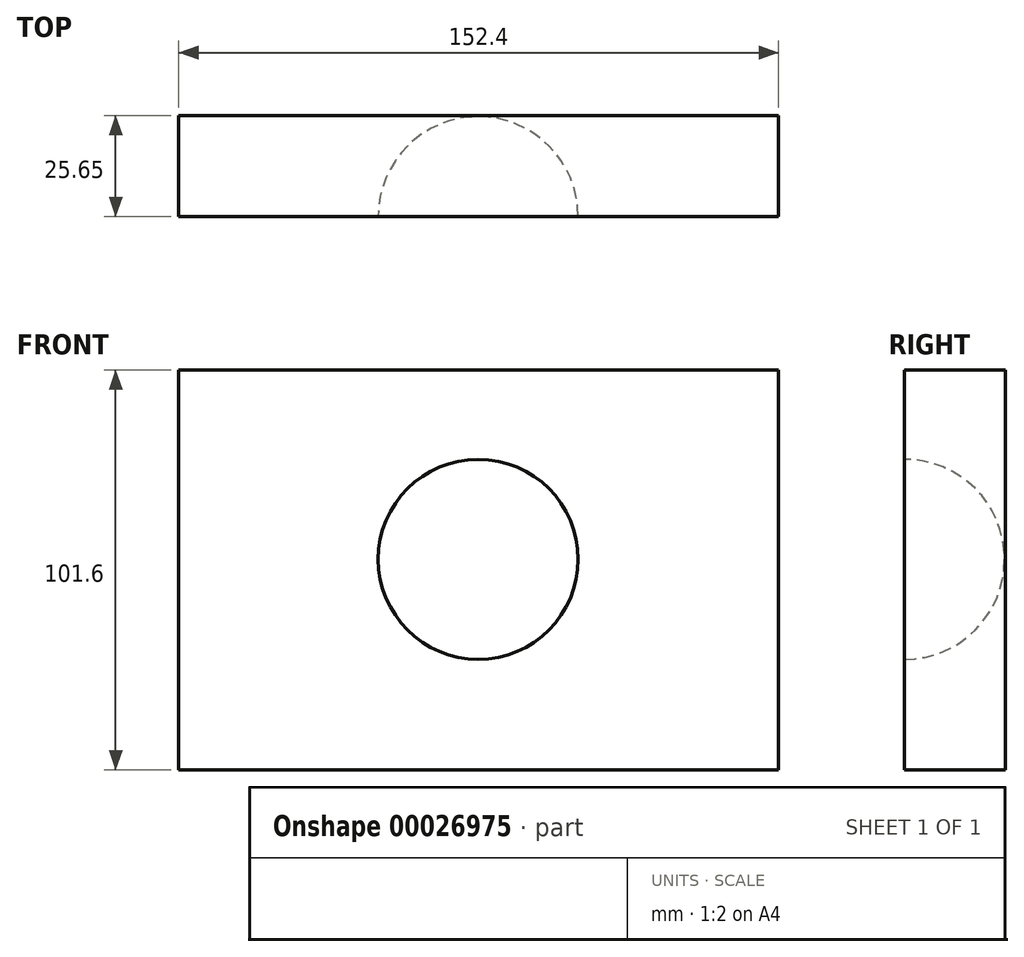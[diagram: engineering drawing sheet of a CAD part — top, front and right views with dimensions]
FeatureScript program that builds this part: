
annotation { "Feature Type Name" : "Feature", "Feature Type Description" : "" }
export const myFeature = defineFeature(function(context is Context, id is Id, definition is map)
    precondition{}
    {
        {
            var Q0;
            Q0=qCreatedBy(makeId("Front.planeOp"),FACE);
            var sketch = newSketch(context, id + "F0", { "sketchPlane" : qUnion([Q0])});
            skLineSegment(sketch, "E0.bottom", {"start": v(-74.85, 56.73) * mm, "end": v(77.55, 56.73) * mm});
            skLineSegment(sketch, "E0.top", {"start": v(-74.85, -44.87) * mm, "end": v(77.55, -44.87) * mm});
            skLineSegment(sketch, "E0.left", {"start": v(-74.85, 56.73) * mm, "end": v(-74.85, -44.87) * mm});
            skLineSegment(sketch, "E0.right", {"start": v(77.55, 56.73) * mm, "end": v(77.55, -44.87) * mm});
            skLineSegment(sketch, "E1", {"start": v(1.35, 23.81) * mm, "end": v(1.35, 23.8) * mm});
            skLineSegment(sketch, "E2.left", {"start": v(1.35, 23.8) * mm, "end": v(1.35, 23.81) * mm});
            skLineSegment(sketch, "E3.bottom", {"start": v(10.34, 5.93) * mm, "end": v(10.34, 5.93) * mm});
            skPoint(sketch, "E4.orphan", {"position": v(1.35, 5.93) * mm});
            skPoint(sketch, "E5.orphan", {"position": v(1.35, 56.73) * mm});
            skPoint(sketch, "E6.orphan", {"position": v(77.55, 5.93) * mm});
            skPoint(sketch, "E7.start.orphan", {"position": v(-74.85, 5.93) * mm});
            skPoint(sketch, "E8.trimOffspring.end.orphan", {"position": v(1.35, -44.87) * mm});
            skSolve(sketch);
        }
        {
            var Q0;
            Q0=makeQuery(id+"F0.imprint","IMPRINT",FACE,{"disambiguationData":[TD([[makeQuery(id+"F0.imprint","IMPRINT",EDGE,{"derivedFrom":sQuery(id+"F0.wireOp",EDGE,"E0.bottom")}),-1.0]])]});
            extrude(context, id + "F1", {"entities" : qUnion([Q0]), "oppositeDirection" : true, "depth" : 25.65 * mm});
        }
        {
            var Q0;
            Q0=makeQuery(id+"F0.imprint","IMPRINT",FACE,{"disambiguationData":[TD([[makeQuery(id+"F0.imprint","IMPRINT",EDGE,{"derivedFrom":sQuery(id+"F0.wireOp",EDGE,"E0.bottom")}),-1.0]])]});
            var sketch = newSketch(context, id + "F2", { "sketchPlane" : qUnion([Q0])});
            skLineSegment(sketch, "E9.bottom", {"start": v(-58.5, 51.11) * mm, "end": v(60.98, 51.11) * mm});
            skLineSegment(sketch, "E9.top", {"start": v(-58.5, -33.83) * mm, "end": v(60.98, -33.83) * mm});
            skLineSegment(sketch, "E9.left", {"start": v(-58.5, 51.11) * mm, "end": v(-58.5, -33.83) * mm});
            skLineSegment(sketch, "E9.right", {"start": v(60.98, 51.11) * mm, "end": v(60.98, -33.83) * mm});
            skLineSegment(sketch, "E10.bottom", {"start": v(1.24, -33.83) * mm, "end": v(1.24, -33.83) * mm});
            skLineSegment(sketch, "E10.top", {"start": v(1.24, 51.11) * mm, "end": v(1.24, 51.11) * mm});
            skLineSegment(sketch, "E10.left", {"start": v(1.24, -16.76) * mm, "end": v(1.24, 34.04) * mm});
            skLineSegment(sketch, "E11.left", {"start": v(-58.5, 8.64) * mm, "end": v(-58.5, 8.64) * mm});
            skLineSegment(sketch, "E11.right", {"start": v(60.98, 8.64) * mm, "end": v(60.98, 8.64) * mm});
            skArc(sketch, "E12", {"start": v(1.24, -16.76) * mm, "mid": v(26.64, 8.64) * mm, "end": v(1.24, 34.04) * mm});
            skSolve(sketch);
        }
        {
            var Q0;
            Q0=makeQuery(id+"F2.imprint","IMPRINT",FACE,{"disambiguationData":[TD([[makeQuery(id+"F2.imprint","IMPRINT",EDGE,{"derivedFrom":sQuery(id+"F2.wireOp",EDGE,"E10.left")}),-1.0]])]});
            var Q1;
            Q1=sQuery(id+"F2.wireOp",EDGE,"E10.left");
            revolve(context, id + "F3", {"operationType" : NewBodyOperationType.REMOVE, "entities" : qUnion([Q0]), "axis" : qUnion([Q1]), "revolveType" : RevolveType.ONE_DIRECTION, "angle" : 180 * degree});
        }
    });
